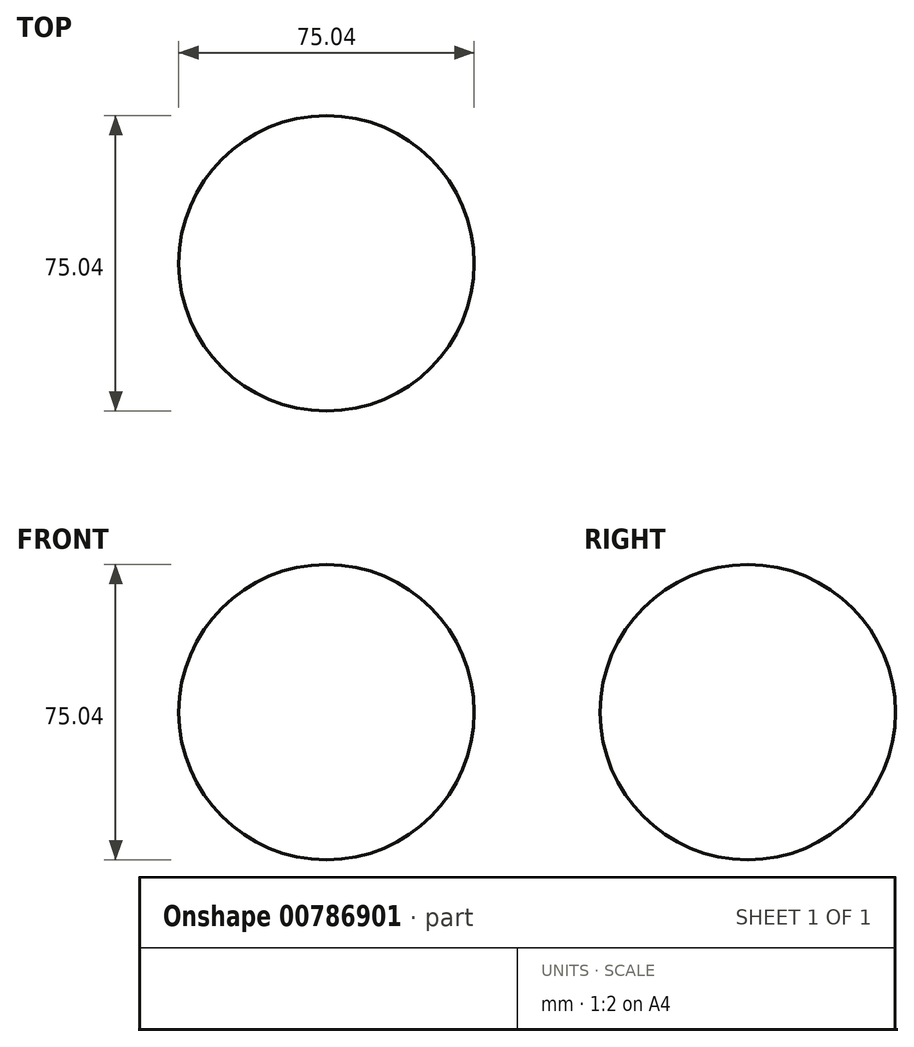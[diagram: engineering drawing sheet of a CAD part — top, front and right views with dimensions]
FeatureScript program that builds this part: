
annotation { "Feature Type Name" : "Feature", "Feature Type Description" : "" }
export const myFeature = defineFeature(function(context is Context, id is Id, definition is map)
    precondition{}
    {
        {
            var Q0;
            Q0=qCreatedBy(makeId("Front.planeOp"),FACE);
            var sketch = newSketch(context, id + "F0", { "sketchPlane" : qUnion([Q0])});
            skCircle(sketch, "E0", {"center": v(0, 0) * mm, "radius": 37.52 * mm});
            skLineSegment(sketch, "E1", {"start": v(0, 65.49) * mm, "end": v(0, -54.54) * mm});
            skSolve(sketch);
        }
        {
            var Q0;
            {var subQ0=sQuery(id+"F0.wireOp",EDGE,"E1");var subQ1=sQuery(id+"F0.wireOp",EDGE,"E0");var subQ2=makeQuery(id+"F0.imprint","INTERSECT",VERTEX,{"disambiguationData":[OD(0.0)],"derivedFrom":[subQ1,subQ0]});Q0=makeQuery(id+"F0.imprint","IMPRINT",FACE,{"disambiguationData":[TD([[makeQuery(id+"F0.imprint","IMPRINT",EDGE,{"disambiguationData":[TD([[subQ2,-1.0]])],"derivedFrom":subQ1}),1.0]])]});}
            var Q1;
            Q1=sQuery(id+"F0.wireOp",EDGE,"E1");
            revolve(context, id + "F1", {"surfaceOperationType" : NewSurfaceOperationType.NEW, "entities" : qUnion([Q0]), "axis" : qUnion([Q1]), "revolveType" : RevolveType.FULL});
        }
    });
